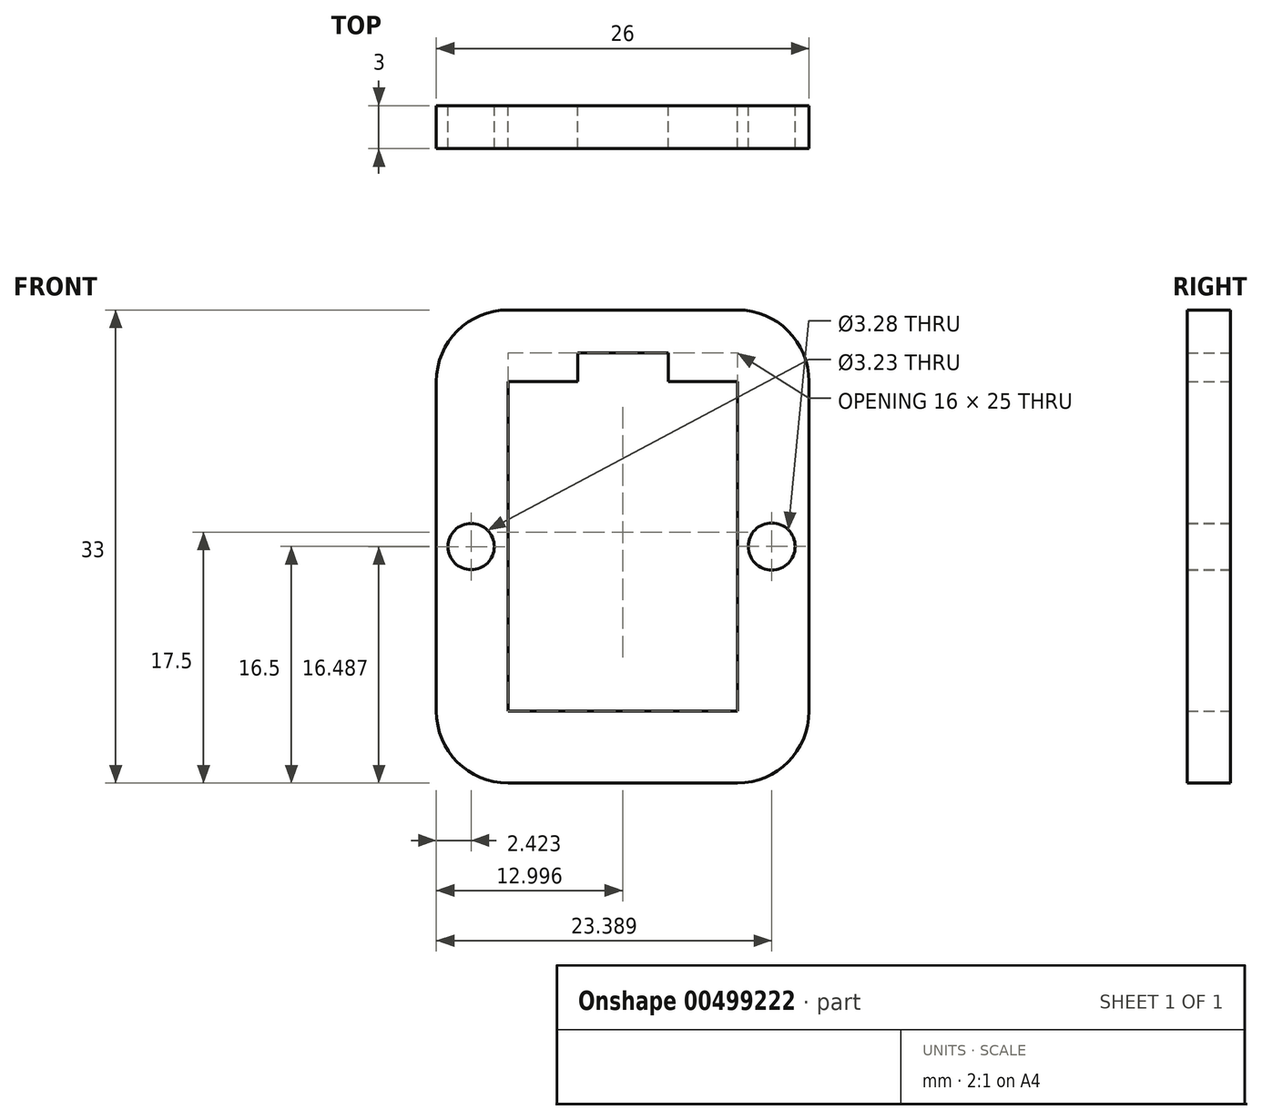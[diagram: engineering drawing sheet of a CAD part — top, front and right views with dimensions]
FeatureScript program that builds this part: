
annotation { "Feature Type Name" : "Feature", "Feature Type Description" : "" }
export const myFeature = defineFeature(function(context is Context, id is Id, definition is map)
    precondition{}
    {
        {
            var Q0;
            Q0=qCreatedBy(makeId("Front.planeOp"),FACE);
            var sketch = newSketch(context, id + "F0", { "sketchPlane" : qUnion([Q0])});
            skLineSegment(sketch, "E0", {"start": v(-39.63, 5) * mm, "end": v(-39.63, 28) * mm});
            skLineSegment(sketch, "E1", {"start": v(-34.63, 33) * mm, "end": v(-18.63, 33) * mm});
            skLineSegment(sketch, "E2", {"start": v(-13.63, 28) * mm, "end": v(-13.63, 5) * mm});
            skLineSegment(sketch, "E3", {"start": v(-18.63, 0) * mm, "end": v(-34.63, 0) * mm});
            skPoint(sketch, "E4.visualSharp", {"position": v(-39.63, 33) * mm});
            skArc(sketch, "E4.filletArc", {"start": v(-34.63, 33) * mm, "mid": v(-38.17, 31.54) * mm, "end": v(-39.63, 28) * mm});
            skPoint(sketch, "E5.visualSharp", {"position": v(-13.63, 33) * mm});
            skArc(sketch, "E5.filletArc", {"start": v(-13.63, 28) * mm, "mid": v(-15.1, 31.54) * mm, "end": v(-18.63, 33) * mm});
            skPoint(sketch, "E6.visualSharp", {"position": v(-39.63, 0) * mm});
            skArc(sketch, "E6.filletArc", {"start": v(-39.63, 5) * mm, "mid": v(-38.17, 1.46) * mm, "end": v(-34.63, 0) * mm});
            skPoint(sketch, "E7.visualSharp", {"position": v(-13.63, 0) * mm});
            skArc(sketch, "E7.filletArc", {"start": v(-18.63, 0) * mm, "mid": v(-15.1, 1.46) * mm, "end": v(-13.63, 5) * mm});
            skLineSegment(sketch, "E8", {"start": v(-34.63, 16.5) * mm, "end": v(-34.63, 5) * mm});
            skPoint(sketch, "E8.startSnap0", {"position": v(-13.63, 16.5) * mm});
            skLineSegment(sketch, "E9", {"start": v(-18.63, 5) * mm, "end": v(-34.63, 5) * mm});
            skLineSegment(sketch, "E10", {"start": v(-18.63, 5) * mm, "end": v(-18.63, 28) * mm});
            skLineSegment(sketch, "E11", {"start": v(-18.63, 28) * mm, "end": v(-23.44, 28) * mm});
            skLineSegment(sketch, "E12", {"start": v(-34.63, 16.5) * mm, "end": v(-34.63, 28) * mm});
            skLineSegment(sketch, "E13", {"start": v(-34.63, 28) * mm, "end": v(-29.78, 28) * mm});
            skLineSegment(sketch, "E14", {"start": v(-29.78, 28) * mm, "end": v(-29.78, 30) * mm});
            skLineSegment(sketch, "E15", {"start": v(-29.78, 30) * mm, "end": v(-23.44, 30) * mm});
            skLineSegment(sketch, "E16", {"start": v(-23.44, 28) * mm, "end": v(-23.44, 30) * mm});
            skCircle(sketch, "E17", {"center": v(-16.24, 16.5) * mm, "radius": 1.64 * mm});
            skCircle(sketch, "E18", {"center": v(-37.2, 16.49) * mm, "radius": 1.61 * mm});
            skSolve(sketch);
        }
        {
            var Q0;
            Q0=makeQuery(id+"F0.imprint","IMPRINT",FACE,{"disambiguationData":[TD([[makeQuery(id+"F0.imprint","IMPRINT",EDGE,{"derivedFrom":sQuery(id+"F0.wireOp",EDGE,"E0")}),-1.0]])]});
            var Q1;
            Q1 = qSketchRegion(id + "F2", true);
            extrude(context, id + "F1", {"entities" : qUnion([Q0, Q1]), "depth" : 3 * mm});
        }
    });
